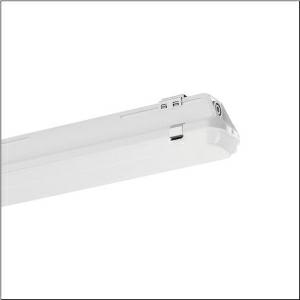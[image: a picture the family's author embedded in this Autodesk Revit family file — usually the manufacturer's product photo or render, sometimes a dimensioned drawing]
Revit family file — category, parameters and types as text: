
# Revit family: monsun_11_emergency_51fp10dp468l2
name_source: partatom
category: Lighting Fixtures
units: mm (PartAtom-declared; Revit-internal decimal feet)

## family parameters
Cut with Voids When Loaded = No
Host = Face
Light Source = No
Part Type = Normal
Room Calculation Point = No
Round Connector Dimension = Use Diameter
Shared = No

## types (1)
- --- (1 x LED, 950 lm, 5.9 W, 4000K)
    Apparent Load = 6 VA
    CIE Flux Codes = 47 77 93 94 100
    Color Rendering = 80
    Color Temperature = 4000K
    Default Elevation = 1800 mm
    Description = Monsun 11 emergency, damp-proof luminaire, chain hanger, primary optical cover: enclosure, of PMMA, light emission: direct distribution, primary light characteristic: symmetric, installation type: suspended mounting, surface-mounted, horizontal mounting, vertical mounting, LED, rated luminous flux: 6.050lm, luminous efficacy: 192lm/W, light colour: 840, colour temperature: 4000K, control gear: DALI 2, with terminal, 5-pole, max. 2.5mm², mains connection: 220..240V, AC/DC, 0/50..60Hz, rated input power: 32W, luminaire housing, of glass-fibre reinforced polyester, uncoated, bright grey, incl. chain hanger, length: 1.590mm, width: 90mm, height: 88mm, clip for enclosure, of stainless steel (V2A), ceiling mounting element, of stainless steel (V2A), chain hanger, of stainless steel (V2A), protection rating (complete): IP66, insulation class (complete): insulation class I (protective earthing), certification: CE, UKCA, protection symbol: D, impact resistance: IK04, permissible operating ambient temperature: -25..+35°C, standard: EN 50419, EN 60598-2-1, EN 60598-2-22, corresponds to IFS (International Featured Standards) requirements for safety and quality in the food industry, for indoor or canopied outdoor use, no direct snow, no direct sun, no direct rain, LABS conformity tested according to VDMA 24364:2018-05, contact your sales advisor before using the luminaires in applications with unclear chemical exposure, large temperature fluctuations or condensation-forming humidity, packaging unit: 1 piece
    Height = 89 mm
    Lamp = 1 x LED
    Lamp Light Flux = 950 lm
    Lamp Power = 5.9 W
    Lamp count = 1
    Length = 1590 mm
    Luminous efficacy = 161 lm/W
    Manufacturer = Siteco
    ModVariant = No
    Model = 51FP10DP468L2
    Mounting Place = Ceiling
    Mounting Type = Surface mounted
    Number of Poles = 1
    OnlyDefault = Yes
    Power Factor = 1
    Product Name = Monsun 11 emergency
    Product group = damp-proof luminaire
    ProductGroupID = 300
    Protection Class = Protection class I
    Protection Degree = IP 66
    RLX_Detail_Level = 1
    RLX_Emergency_Light_Flux = 0 lm
    RLX_Emergency_Type = 0
    RLX_Emergency_Type_DB = No
    RlxData = <blob elided: 92665 chars, md5=0d827b2b>
    Socket = socket
    Standby Power = 0 W
    System Light Flux = 950 lm
    System Power = 6 W
    Type Comments = : DC mode (central or group accumulator) initial emergency light level
    Type Image = l_1349237.jpg
    URL = http://relux.com
    VarID = @adj_033853
    Voltage = 0 V
    Weight = 0.00 kg
    Width = 90 mm

## geometry (parser evidence)
native form markers: Blend x4, Sweep x15
no freeform markers — native parametric forms only
